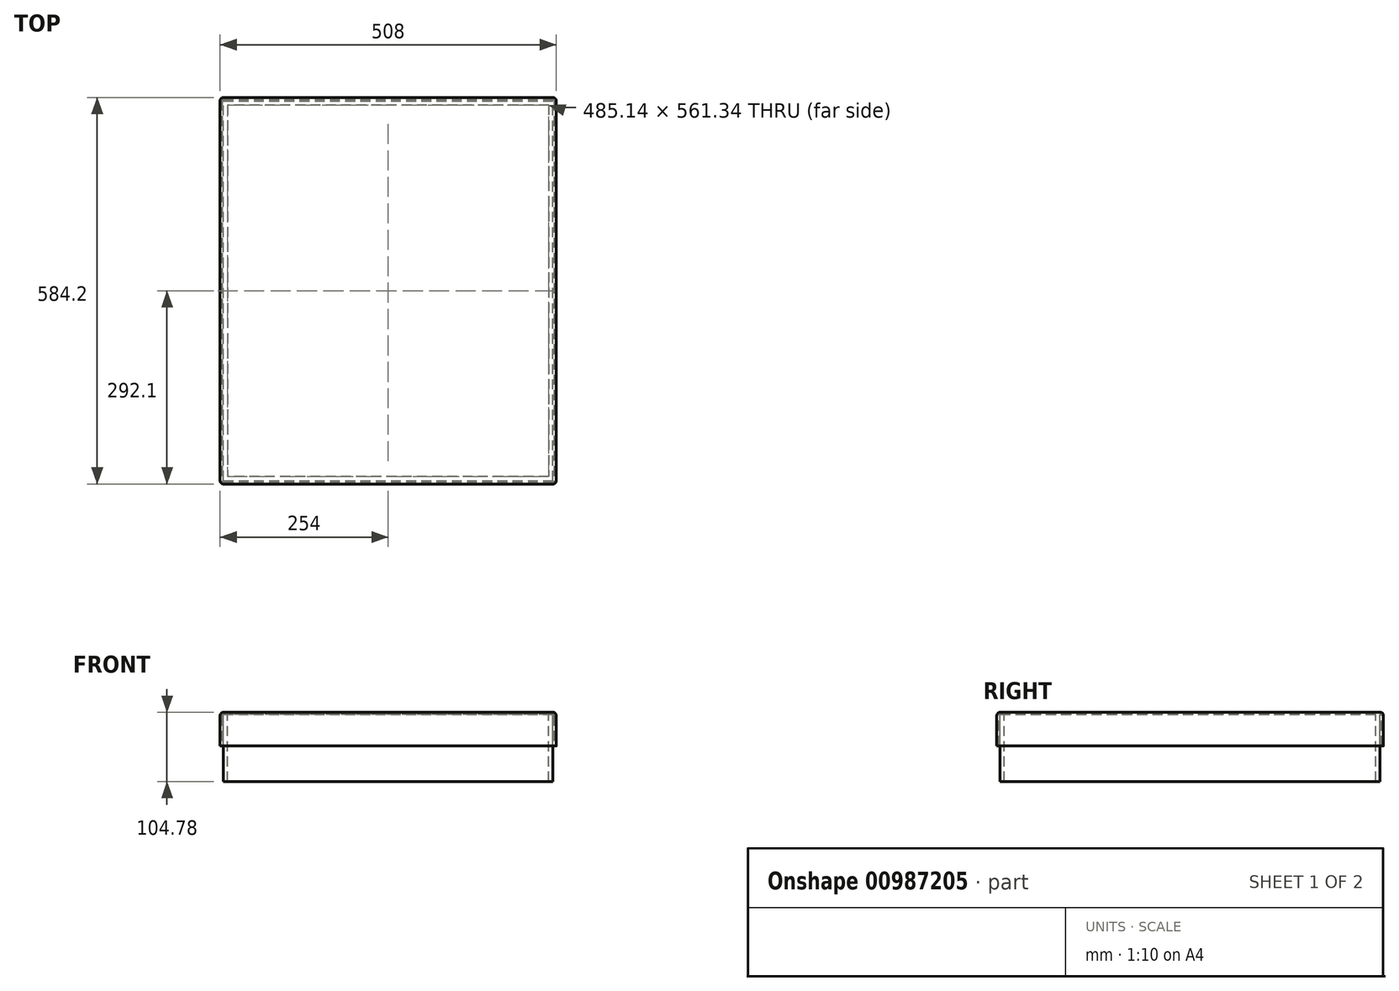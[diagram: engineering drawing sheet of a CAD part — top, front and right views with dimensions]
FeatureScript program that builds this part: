
annotation { "Feature Type Name" : "Feature", "Feature Type Description" : "" }
export const myFeature = defineFeature(function(context is Context, id is Id, definition is map)
    precondition{}
    {
        {
            var Q0;
            Q0=qCreatedBy(makeId("Top.planeOp"),FACE);
            var sketch = newSketch(context, id + "F0", { "sketchPlane" : qUnion([Q0])});
            skLineSegment(sketch, "E0.bottom", {"start": v(-254, 292.1) * mm, "end": v(254, 292.1) * mm});
            skLineSegment(sketch, "E0.top", {"start": v(-254, -292.1) * mm, "end": v(254, -292.1) * mm});
            skLineSegment(sketch, "E0.left", {"start": v(-254, 292.1) * mm, "end": v(-254, -292.1) * mm});
            skLineSegment(sketch, "E0.right", {"start": v(254, 292.1) * mm, "end": v(254, -292.1) * mm});
            skSolve(sketch);
        }
        {
            var Q0;
            Q0=makeQuery(id+"F0.imprint","IMPRINT",FACE,{"disambiguationData":[TD([[makeQuery(id+"F0.imprint","IMPRINT",EDGE,{"derivedFrom":sQuery(id+"F0.wireOp",EDGE,"E0.bottom")}),-1.0]])]});
            extrude(context, id + "F1", {"entities" : qUnion([Q0]), "depth" : 50.8 * mm, "offsetDistance" : 25.4 * mm});
        }
        {
            var Q0;
            Q0=makeQuery(id+"F1.opExtrude","SWEPT_EDGE",EDGE,{"disambiguationData":[OSD([sQuery(id+"F0.wireOp",EDGE,"E0.top"),sQuery(id+"F0.wireOp",EDGE,"E0.left")])]});
            var Q1;
            Q1=makeQuery(id+"F1.opExtrude","CAP_EDGE",EDGE,{"disambiguationData":[OSD([sQuery(id+"F0.wireOp",EDGE,"E0.left")])],"isStart":false});
            var Q2;
            Q2=makeQuery(id+"F1.opExtrude","CAP_FACE",FACE,{"disambiguationData":[OSD([sQuery(id+"F0.wireOp",EDGE,"E0.bottom"),sQuery(id+"F0.wireOp",EDGE,"E0.top"),sQuery(id+"F0.wireOp",EDGE,"E0.left"),sQuery(id+"F0.wireOp",EDGE,"E0.right")])],"isStart":false});
            var Q3;
            Q3=makeQuery(id+"F1.opExtrude","SWEPT_EDGE",EDGE,{"disambiguationData":[OSD([sQuery(id+"F0.wireOp",EDGE,"E0.top"),sQuery(id+"F0.wireOp",EDGE,"E0.right")])]});
            var Q4;
            Q4=makeQuery(id+"F1.opExtrude","SWEPT_EDGE",EDGE,{"disambiguationData":[OSD([sQuery(id+"F0.wireOp",EDGE,"E0.bottom"),sQuery(id+"F0.wireOp",EDGE,"E0.right")])]});
            var Q5;
            Q5=makeQuery(id+"F1.opExtrude","SWEPT_EDGE",EDGE,{"disambiguationData":[OSD([sQuery(id+"F0.wireOp",EDGE,"E0.bottom"),sQuery(id+"F0.wireOp",EDGE,"E0.left")])]});
            fillet(context, id + "F2", {"entities" : qUnion([Q0, Q1, Q2, Q3, Q4, Q5]), "radius" : 5.08 * mm, "tangentPropagation" : true, "allowEdgeOverflow" : false});
        }
        {
            var Q0;
            Q0=makeQuery(id+"F1.opExtrude","CAP_FACE",FACE,{"disambiguationData":[OSD([sQuery(id+"F0.wireOp",EDGE,"E0.bottom"),sQuery(id+"F0.wireOp",EDGE,"E0.top"),sQuery(id+"F0.wireOp",EDGE,"E0.left"),sQuery(id+"F0.wireOp",EDGE,"E0.right")])],"isStart":true});
            shell(context, id + "F3", {"entities" : qUnion([Q0]), "thickness" : 3.17 * mm});
        }
        {
            var Q0;
            Q0=makeQuery(id+"F3.opShell","OFFSET_FACE",FACE,{"disambiguationData":[OSD([sQuery(id+"F0.wireOp",EDGE,"E0.bottom"),sQuery(id+"F0.wireOp",EDGE,"E0.top"),sQuery(id+"F0.wireOp",EDGE,"E0.left"),sQuery(id+"F0.wireOp",EDGE,"E0.right")])]});
            var sketch = newSketch(context, id + "F4", { "sketchPlane" : qUnion([Q0])});
            skLineSegment(sketch, "E1.0.0", {"start": v(248.92, 287.02) * mm, "end": v(-248.92, 287.02) * mm});
            skLineSegment(sketch, "E1.0.1", {"start": v(-248.92, -287.02) * mm, "end": v(-248.92, 287.02) * mm});
            skLineSegment(sketch, "E1.0.2", {"start": v(248.92, -287.02) * mm, "end": v(-248.92, -287.02) * mm});
            skLineSegment(sketch, "E1.0.3", {"start": v(248.92, -287.02) * mm, "end": v(248.92, 287.02) * mm});
            skLineSegment(sketch, "E2.0", {"start": v(242.57, 280.67) * mm, "end": v(-242.57, 280.67) * mm});
            skLineSegment(sketch, "E2.1", {"start": v(242.57, -280.67) * mm, "end": v(242.57, 280.67) * mm});
            skLineSegment(sketch, "E2.2", {"start": v(242.57, -280.67) * mm, "end": v(-242.57, -280.67) * mm});
            skLineSegment(sketch, "E2.3", {"start": v(-242.57, -280.67) * mm, "end": v(-242.57, 280.67) * mm});
            skSolve(sketch);
        }
        {
            var Q0;
            Q0 = qSketchRegion(id + "F4", true);
            extrude(context, id + "F5", {"entities" : qUnion([Q0]), "depth" : 101.6 * mm, "offsetDistance" : 25.4 * mm});
        }
    });
